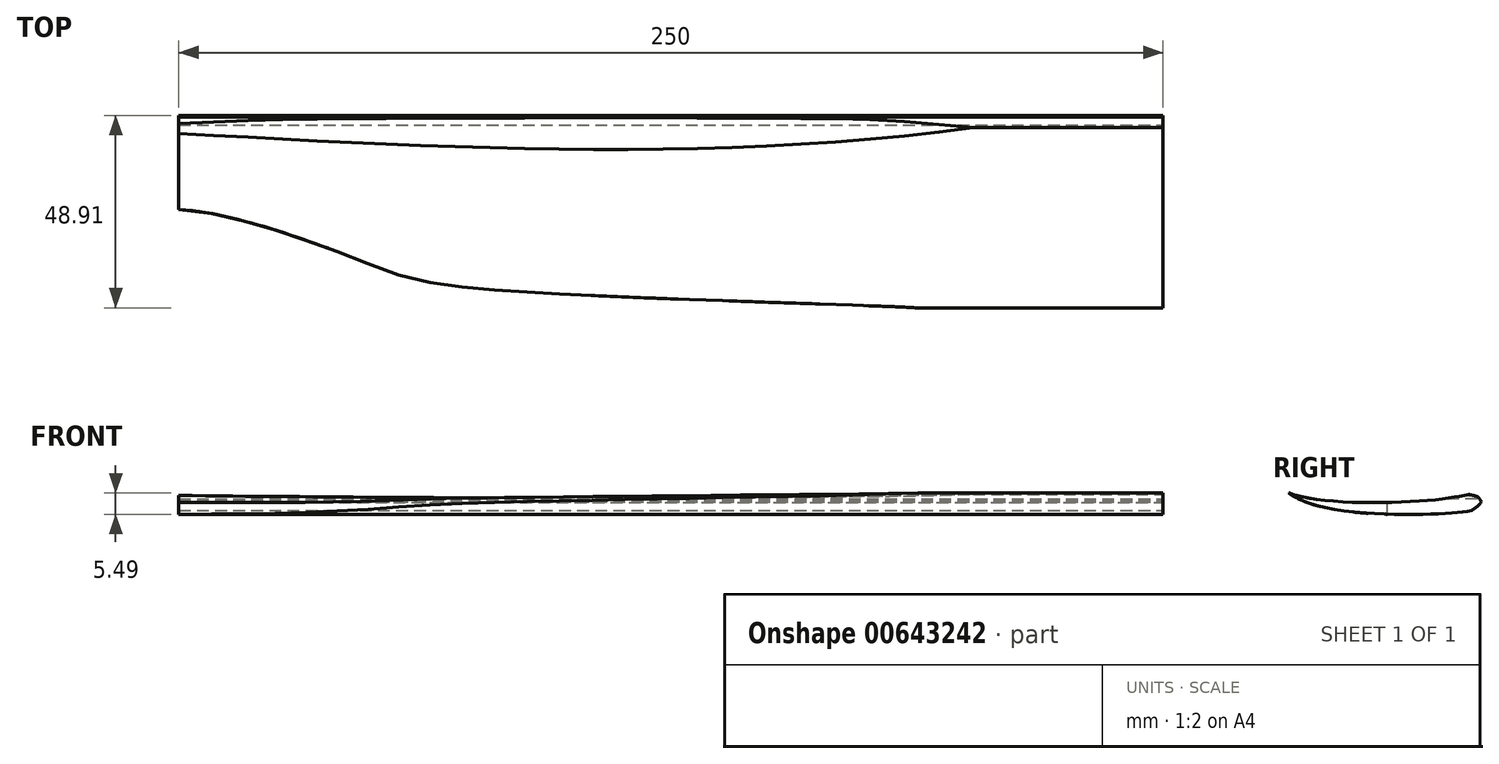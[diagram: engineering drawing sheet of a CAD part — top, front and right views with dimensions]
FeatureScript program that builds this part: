
annotation { "Feature Type Name" : "Feature", "Feature Type Description" : "" }
export const myFeature = defineFeature(function(context is Context, id is Id, definition is map)
    precondition{}
    {
        {
            var Q0;
            Q0=qCreatedBy(makeId("Front.planeOp"),FACE);
            var sketch = newSketch(context, id + "F0", { "sketchPlane" : qUnion([Q0])});
            skLineSegment(sketch, "E0.bottom", {"start": v(-250, 4.12) * mm, "end": v(0, 4.12) * mm});
            skLineSegment(sketch, "E0.top", {"start": v(-250, -5.88) * mm, "end": v(0, -5.88) * mm});
            skLineSegment(sketch, "E0.left", {"start": v(-250, 4.12) * mm, "end": v(-250, -5.88) * mm});
            skLineSegment(sketch, "E0.right", {"start": v(0, 4.12) * mm, "end": v(0, -5.88) * mm});
            skSolve(sketch);
        }
        {
            var Q0;
            Q0 = qSketchRegion(id + "F0", true);
            extrude(context, id + "F1", {"entities" : qUnion([Q0]), "depth" : 50 * mm, "offsetDistance" : 25 * mm});
        }
        {
            var Q0;
            Q0=qCreatedBy(makeId("Front.planeOp"),FACE);
            var sketch = newSketch(context, id + "F2", { "sketchPlane" : qUnion([Q0])});
            skFitSpline(sketch, "E1", {"points": [v(-313.29, 0) * mm, v(-36.17, 0) * mm, v(0.99, 4.4) * mm, v(-313.48, 5.06) * mm], "startDerivative": vector(55.07, 1.82) * mm, "endDerivative": vector(2.69, 6.59) * mm});
            skLineSegment(sketch, "E2", {"start": v(-313.29, 0) * mm, "end": v(-313.29, 8.7) * mm});
            skLineSegment(sketch, "E3", {"start": v(-313.29, 8.7) * mm, "end": v(-313.29, 8.7) * mm});
            skLineSegment(sketch, "E4", {"start": v(-313.29, 8.7) * mm, "end": v(-313.48, 5.06) * mm});
            skSolve(sketch);
        }
        {
            var Q0;
            Q0 = qSketchRegion(id + "F2", true);
            extrude(context, id + "F3", {"entities" : qUnion([Q0]), "operationType" : NewBodyOperationType.REMOVE, "depth" : 30 * mm, "offsetDistance" : 25 * mm});
        }
        {
            var Q0;
            Q0=qCreatedBy(makeId("Right.planeOp"),FACE);
            var sketch = newSketch(context, id + "F4", { "sketchPlane" : qUnion([Q0])});
            skFitSpline(sketch, "E5", {"points": [v(0.17, 0.27) * mm, v(-12.73, -1.79) * mm, v(-49.4, 0) * mm], "startDerivative": vector(-25.73, -3.37) * mm, "endDerivative": vector(-34.92, 14.17) * mm});
            skFitSpline(sketch, "E6", {"points": [v(0.65, -3.5) * mm, v(-11.87, -5.33) * mm, v(-49.4, 0) * mm], "startDerivative": vector(-28.12, -9.5) * mm, "endDerivative": vector(-33.6, 27.02) * mm});
            skLineSegment(sketch, "E7", {"start": v(0.57, -1.34) * mm, "end": v(0.17, 0.27) * mm});
            skLineSegment(sketch, "E8", {"start": v(0.57, -1.34) * mm, "end": v(0.65, -3.5) * mm});
            skSolve(sketch);
        }
        {
            var Q0;
            Q0 = qSketchRegion(id + "F4", true);
            extrude(context, id + "F5", {"entities" : qUnion([Q0]), "operationType" : NewBodyOperationType.INTERSECT, "oppositeDirection" : true, "depth" : 250 * mm, "offsetDistance" : 25 * mm});
        }
        {
            var Q0;
            Q0=qCreatedBy(makeId("Right.planeOp"),FACE);
            var sketch = newSketch(context, id + "F6", { "sketchPlane" : qUnion([Q0])});
            skFitSpline(sketch, "E9", {"points": [v(0, -2.16) * mm, v(-0.93, -1.56) * mm, v(-1.57, -0.93) * mm, v(-4.24, 0) * mm, v(-1.25, 1.96) * mm, v(2.18, 1.57) * mm, v(1.06, -1.32) * mm, v(0, -2.16) * mm]});
            skFitSpline(sketch, "E10", {"points": [v(-3.18, -4.68) * mm, v(-1.54, -3.48) * mm, v(-0.37, -2.28) * mm, v(0, -2.16) * mm], "startDerivative": vector(1.26, 1.8) * mm, "endDerivative": vector(1.32, 1.43) * mm});
            skFitSpline(sketch, "E11", {"points": [v(0, -2.16) * mm, v(1.05, -2.24) * mm, v(1.2, -2.7) * mm, v(-0.72, -4.2) * mm, v(-3.18, -4.68) * mm], "startDerivative": vector(5.22, 0.3) * mm, "endDerivative": vector(-3.24, 2.28) * mm});
            skFitSpline(sketch, "E12", {"points": [v(-0.37, -2.28) * mm, v(-0.55, -2.07) * mm, v(-0.73, -1.8) * mm, v(-0.93, -1.56) * mm], "startDerivative": vector(-0.15, 0.66) * mm, "endDerivative": vector(-0.27, 0.8) * mm});
            skLineSegment(sketch, "E13", {"start": v(-0.55, -2.07) * mm, "end": v(-0.5, -2.36) * mm});
            skSolve(sketch);
        }
        {
            var Q0;
            Q0 = qSketchRegion(id + "F6", true);
            extrude(context, id + "F7", {"entities" : qUnion([Q0]), "operationType" : NewBodyOperationType.REMOVE, "oppositeDirection" : true, "depth" : 250 * mm, "offsetDistance" : 25 * mm});
        }
        {
            var Q0;
            Q0 = qSketchRegion(id + "F6", true);
            extrude(context, id + "F8", {"entities" : qUnion([Q0]), "operationType" : NewBodyOperationType.REMOVE, "oppositeDirection" : true, "depth" : 60 * mm, "offsetDistance" : 25 * mm});
        }
        {
            var Q0;
            Q0=qCreatedBy(makeId("Top.planeOp"),FACE);
            var sketch = newSketch(context, id + "F9", { "sketchPlane" : qUnion([Q0])});
            skFitSpline(sketch, "E14", {"points": [v(-56.83, -50.07) * mm, v(-173.99, -44.46) * mm, v(-208.66, -35.53) * mm, v(-259.13, -26.95) * mm, v(-252.43, -49.16) * mm, v(-249.55, -52.13) * mm, v(-235.37, -53.21) * mm, v(-56.83, -50.07) * mm]});
            skSolve(sketch);
        }
        {
            var Q0;
            Q0 = qSketchRegion(id + "F9", true);
            extrude(context, id + "F10", {"entities" : qUnion([Q0]), "operationType" : NewBodyOperationType.REMOVE, "oppositeDirection" : true, "depth" : 25 * mm, "offsetDistance" : 25 * mm});
        }
        {
            var Q0;
            Q0 = qSketchRegion(id + "F6", true);
            extrude(context, id + "F11", {"entities" : qUnion([Q0]), "operationType" : NewBodyOperationType.REMOVE, "oppositeDirection" : true, "depth" : 60 * mm, "offsetDistance" : 25 * mm});
        }
    });
